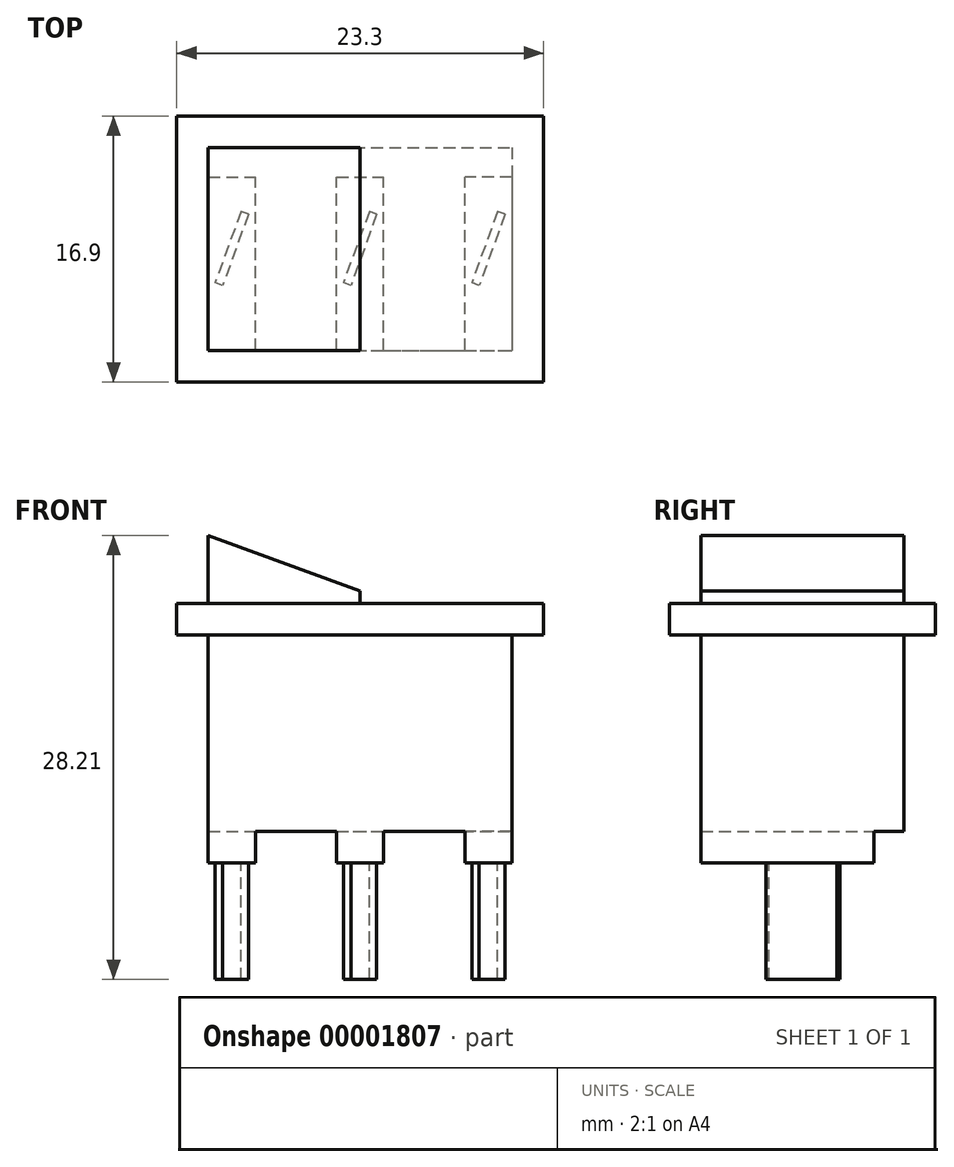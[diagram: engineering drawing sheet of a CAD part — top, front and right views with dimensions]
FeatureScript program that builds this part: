
annotation { "Feature Type Name" : "Feature", "Feature Type Description" : "" }
export const myFeature = defineFeature(function(context is Context, id is Id, definition is map)
    precondition{}
    {
        {
            var Q0;
            Q0=qCreatedBy(makeId("Top.planeOp"),FACE);
            var sketch = newSketch(context, id + "F0", { "sketchPlane" : qUnion([Q0])});
            skLineSegment(sketch, "E0.bottom", {"start": v(-12.09, 6.42) * mm, "end": v(7.21, 6.42) * mm});
            skLineSegment(sketch, "E0.top", {"start": v(-12.09, -6.48) * mm, "end": v(7.21, -6.48) * mm});
            skLineSegment(sketch, "E0.left", {"start": v(-12.09, 6.42) * mm, "end": v(-12.09, -6.48) * mm});
            skLineSegment(sketch, "E0.right", {"start": v(7.21, 6.42) * mm, "end": v(7.21, -6.48) * mm});
            skSolve(sketch);
        }
        {
            var Q0;
            Q0=qSketchRegion(id+"F0",true);
            extrude(context, id + "F1", {"entities" : qUnion([Q0]), "depth" : 12.5 * mm});
        }
        {
            var Q0;
            Q0=makeQuery(id+"F1.opExtrude","CAP_FACE",FACE,{"disambiguationData":[OSD([sQuery(id+"F0.wireOp",EDGE,"E0.bottom"),sQuery(id+"F0.wireOp",EDGE,"E0.top"),sQuery(id+"F0.wireOp",EDGE,"E0.left"),sQuery(id+"F0.wireOp",EDGE,"E0.right")])],"isStart":false});
            var sketch = newSketch(context, id + "F2", { "sketchPlane" : qUnion([Q0])});
            skLineSegment(sketch, "E1.bottom", {"start": v(-14.09, 8.42) * mm, "end": v(9.21, 8.42) * mm});
            skLineSegment(sketch, "E1.top", {"start": v(-14.09, -8.48) * mm, "end": v(9.21, -8.48) * mm});
            skLineSegment(sketch, "E1.left", {"start": v(-14.09, 8.42) * mm, "end": v(-14.09, -8.48) * mm});
            skLineSegment(sketch, "E1.right", {"start": v(9.21, 8.42) * mm, "end": v(9.21, -8.48) * mm});
            skSolve(sketch);
        }
        {
            var Q0;
            Q0=qSketchRegion(id+"F2",true);
            extrude(context, id + "F3", {"entities" : qUnion([Q0]), "operationType" : NewBodyOperationType.ADD, "depth" : 2 * mm});
        }
        {
            var Q0;
            Q0=makeQuery(id+"F1.opExtrude","CAP_FACE",FACE,{"disambiguationData":[OSD([sQuery(id+"F0.wireOp",EDGE,"E0.bottom"),sQuery(id+"F0.wireOp",EDGE,"E0.top"),sQuery(id+"F0.wireOp",EDGE,"E0.left"),sQuery(id+"F0.wireOp",EDGE,"E0.right")])],"isStart":true});
            var sketch = newSketch(context, id + "F4", { "sketchPlane" : qUnion([Q0])});
            skLineSegment(sketch, "E2", {"start": v(-12.09, 0.03) * mm, "end": v(7.21, 0.03) * mm, "construction": true});
            skLineSegment(sketch, "E3.bottom", {"start": v(-12.09, 6.48) * mm, "end": v(-9.09, 6.48) * mm});
            skLineSegment(sketch, "E3.top", {"start": v(-12.09, -4.52) * mm, "end": v(-9.09, -4.52) * mm});
            skLineSegment(sketch, "E3.left", {"start": v(-12.09, 6.48) * mm, "end": v(-12.09, -4.52) * mm});
            skLineSegment(sketch, "E3.right", {"start": v(-9.09, 6.48) * mm, "end": v(-9.09, -4.52) * mm});
            skLineSegment(sketch, "E4.bottom", {"start": v(-3.94, 6.48) * mm, "end": v(-0.94, 6.48) * mm});
            skLineSegment(sketch, "E4.top", {"start": v(-3.94, -4.52) * mm, "end": v(-0.94, -4.52) * mm});
            skLineSegment(sketch, "E4.left", {"start": v(-3.94, 6.48) * mm, "end": v(-3.94, -4.52) * mm});
            skLineSegment(sketch, "E4.right", {"start": v(-0.94, 6.48) * mm, "end": v(-0.94, -4.52) * mm});
            skLineSegment(sketch, "E5.bottom", {"start": v(7.21, 6.48) * mm, "end": v(4.21, 6.48) * mm});
            skLineSegment(sketch, "E5.top", {"start": v(7.21, -4.52) * mm, "end": v(4.21, -4.52) * mm});
            skLineSegment(sketch, "E5.left", {"start": v(7.21, 6.48) * mm, "end": v(7.21, -4.52) * mm});
            skLineSegment(sketch, "E5.right", {"start": v(4.21, 6.48) * mm, "end": v(4.21, -4.52) * mm});
            skPoint(sketch, "E6", {"position": v(-2.44, -4.52) * mm});
            skPoint(sketch, "E7", {"position": v(-2.44, 0.03) * mm});
            skSolve(sketch);
        }
        {
            var Q0;
            Q0=qSketchRegion(id+"F4",true);
            extrude(context, id + "F5", {"entities" : qUnion([Q0]), "operationType" : NewBodyOperationType.ADD, "depth" : 2 * mm});
        }
        {
            var Q0;
            Q0=makeQuery(id+"F5.opExtrude","CAP_FACE",FACE,{"disambiguationData":[OSD([sQuery(id+"F4.wireOp",EDGE,"E3.bottom"),sQuery(id+"F4.wireOp",EDGE,"E3.top"),sQuery(id+"F4.wireOp",EDGE,"E3.left"),sQuery(id+"F4.wireOp",EDGE,"E3.right")])],"isStart":false});
            var sketch = newSketch(context, id + "F6", { "sketchPlane" : qUnion([Q0])});
            skLineSegment(sketch, "E8", {"start": v(-12.09, 0) * mm, "end": v(-9.09, 0) * mm, "construction": true});
            skLineSegment(sketch, "E9.rect.bottom", {"start": v(-9.53, -2.17) * mm, "end": v(-10, -2.34) * mm});
            skLineSegment(sketch, "E9.rect.top", {"start": v(-11.17, 2.34) * mm, "end": v(-11.64, 2.17) * mm});
            skLineSegment(sketch, "E9.rect.left", {"start": v(-9.53, -2.17) * mm, "end": v(-11.17, 2.34) * mm});
            skLineSegment(sketch, "E9.rect.right", {"start": v(-10, -2.34) * mm, "end": v(-11.64, 2.17) * mm});
            skPoint(sketch, "E9.rect.middle", {"position": v(-10.59, 0) * mm});
            skLineSegment(sketch, "E10.1.0.0", {"start": v(-3.02, 2.34) * mm, "end": v(-3.5, 2.17) * mm});
            skLineSegment(sketch, "E10.1.0.1", {"start": v(-1.38, -2.17) * mm, "end": v(-3.02, 2.34) * mm});
            skLineSegment(sketch, "E10.1.0.2", {"start": v(-1.85, -2.34) * mm, "end": v(-3.5, 2.17) * mm});
            skLineSegment(sketch, "E10.1.0.3", {"start": v(-1.38, -2.17) * mm, "end": v(-1.85, -2.34) * mm});
            skLineSegment(sketch, "E10.2.0.0", {"start": v(5.13, 2.34) * mm, "end": v(4.66, 2.17) * mm});
            skLineSegment(sketch, "E10.2.0.1", {"start": v(6.77, -2.17) * mm, "end": v(5.13, 2.34) * mm});
            skLineSegment(sketch, "E10.2.0.2", {"start": v(6.3, -2.34) * mm, "end": v(4.66, 2.17) * mm});
            skLineSegment(sketch, "E10.2.0.3", {"start": v(6.77, -2.17) * mm, "end": v(6.3, -2.34) * mm});
            skLineSegment(sketch, "E10.direction1", {"start": v(-11.64, 2.17) * mm, "end": v(-3.5, 2.17) * mm, "construction": true});
            skSolve(sketch);
        }
        {
            var Q0;
            Q0=qSketchRegion(id+"F6",true);
            extrude(context, id + "F7", {"entities" : qUnion([Q0]), "operationType" : NewBodyOperationType.ADD, "depth" : 7.4 * mm});
        }
        {
            var Q0;
            Q0=makeQuery(id+"F3.opExtrude","CAP_FACE",FACE,{"disambiguationData":[OSD([sQuery(id+"F2.wireOp",EDGE,"E1.bottom"),sQuery(id+"F2.wireOp",EDGE,"E1.top"),sQuery(id+"F2.wireOp",EDGE,"E1.left"),sQuery(id+"F2.wireOp",EDGE,"E1.right")])],"isStart":false});
            var sketch = newSketch(context, id + "F8", { "sketchPlane" : qUnion([Q0])});
            skLineSegment(sketch, "E11.bottom", {"start": v(-12.09, 6.42) * mm, "end": v(7.21, 6.42) * mm});
            skLineSegment(sketch, "E11.top", {"start": v(-12.09, -6.48) * mm, "end": v(7.21, -6.48) * mm});
            skLineSegment(sketch, "E11.left", {"start": v(-12.09, 6.42) * mm, "end": v(-12.09, -6.48) * mm});
            skLineSegment(sketch, "E11.right", {"start": v(7.21, 6.42) * mm, "end": v(7.21, -6.48) * mm});
            skLineSegment(sketch, "E12", {"start": v(-2.44, 6.42) * mm, "end": v(-2.44, -6.48) * mm});
            skSolve(sketch);
        }
        {
            var Q0;
            {var subQ1=sQuery(id+"F8.wireOp",EDGE,"E11.left");Q0=makeQuery(id+"F8.imprint","IMPRINT",FACE,{"disambiguationData":[TD([[makeQuery(id+"F8.imprint","IMPRINT",EDGE,{"derivedFrom":subQ1}),1.0]])]});}
            extrude(context, id + "F9", {"entities" : qUnion([Q0]), "operationType" : NewBodyOperationType.ADD, "depth" : 5.8 * mm});
        }
        {
            var Q0;
            Q0=makeQuery(id+"F9.opExtrude","CAP_EDGE",EDGE,{"disambiguationData":[OSD([sQuery(id+"F8.wireOp",EDGE,"E12")])],"isStart":false});
            chamfer(context, id + "F10", {"entities" : qUnion([Q0]), "chamferType" : ChamferType.OFFSET_ANGLE, "width" : 5 * mm, "oppositeDirection" : false, "angle" : 70 * degree});
        }
    });
